FCSTD DOCUMENT  (FreeCAD 0.19R)
Label: SpokePattern32
License: All rights reserved
LicenseURL: http://en.wikipedia.org/wiki/All_rights_reserved
objects: Sketcher::SketchObject×1
note: 1 computed .brp shape members not serialized (recipe doc carries the construction recipe); baked Part::Feature solids carry a one-line shape summary decoded from their .brp

FEATURE [Sketcher::SketchObject] Sketch
  FullyConstrained = false
  sketch-geometry (69):
    g0: Circle CenterX=30 CenterY=0 CenterZ=0 NormalX=0 NormalY=0 NormalZ=1 AngleXU=0 Radius=1.25
    g1: Circle CenterX=21.2132 CenterY=21.2132 CenterZ=0 NormalX=0 NormalY=0 NormalZ=1 AngleXU=0 Radius=1.25
    g2: Circle CenterX=11.4805 CenterY=27.7164 CenterZ=0 NormalX=0 NormalY=0 NormalZ=1 AngleXU=0 Radius=1.25
    g3: Circle CenterX=0 CenterY=30 CenterZ=0 NormalX=0 NormalY=0 NormalZ=1 AngleXU=0 Radius=1.25
    g4: Circle CenterX=1.54e-14 CenterY=-30 CenterZ=0 NormalX=0 NormalY=0 NormalZ=1 AngleXU=0 Radius=1.25
    g5: Circle CenterX=-27.7164 CenterY=11.4805 CenterZ=0 NormalX=0 NormalY=0 NormalZ=1 AngleXU=0 Radius=1.25
    g6: Circle CenterX=-27.7164 CenterY=-11.4805 CenterZ=0 NormalX=0 NormalY=0 NormalZ=1 AngleXU=0 Radius=1.25
    g7: Circle CenterX=-11.4805 CenterY=27.7164 CenterZ=0 NormalX=0 NormalY=0 NormalZ=1 AngleXU=0 Radius=1.25
    g8: Circle CenterX=-30 CenterY=-3.2e-15 CenterZ=0 NormalX=0 NormalY=0 NormalZ=1 AngleXU=0 Radius=1.25
    g9: Circle CenterX=-21.2132 CenterY=-21.2132 CenterZ=0 NormalX=0 NormalY=0 NormalZ=1 AngleXU=0 Radius=1.25
    g10: Circle CenterX=-11.4805 CenterY=-27.7164 CenterZ=0 NormalX=0 NormalY=0 NormalZ=1 AngleXU=0 Radius=1.25
    g11: Circle CenterX=11.4805 CenterY=-27.7164 CenterZ=0 NormalX=0 NormalY=0 NormalZ=1 AngleXU=0 Radius=1.25
    g12: Circle CenterX=21.2132 CenterY=-21.2132 CenterZ=0 NormalX=0 NormalY=0 NormalZ=1 AngleXU=0 Radius=1.25
    g13: Circle CenterX=27.7164 CenterY=-11.4805 CenterZ=0 NormalX=0 NormalY=0 NormalZ=1 AngleXU=0 Radius=1.25
    g14: Circle CenterX=30 CenterY=1.24e-14 CenterZ=0 NormalX=0 NormalY=0 NormalZ=1 AngleXU=0 Radius=1.25
    g15: Circle CenterX=27.7164 CenterY=11.4805 CenterZ=0 NormalX=0 NormalY=0 NormalZ=1 AngleXU=0 Radius=1.25
    g16: Circle CenterX=0 CenterY=0 CenterZ=0 NormalX=0 NormalY=0 NormalZ=1 AngleXU=0 Radius=30
    g17: LineSegment StartX=-11.4805 StartY=27.7164 StartZ=0 EndX=0 EndY=0 EndZ=0
    g18: LineSegment StartX=-27.7164 StartY=11.4805 StartZ=0 EndX=0 EndY=0 EndZ=0
    g19: LineSegment StartX=21.2132 StartY=-21.2132 StartZ=0 EndX=0 EndY=0 EndZ=0
    g20: LineSegment StartX=27.7164 StartY=-11.4805 StartZ=0 EndX=0 EndY=0 EndZ=0
    g21: LineSegment StartX=30 StartY=1.24e-14 StartZ=0 EndX=0 EndY=0 EndZ=0
    g22: LineSegment StartX=27.7164 StartY=11.4805 StartZ=0 EndX=0 EndY=0 EndZ=0
    g23: LineSegment StartX=30 StartY=0 StartZ=0 EndX=0 EndY=0 EndZ=0
    g24: LineSegment StartX=11.4805 StartY=27.7164 StartZ=0 EndX=0 EndY=0 EndZ=0
    g25: LineSegment StartX=0 StartY=30 StartZ=0 EndX=0 EndY=0 EndZ=0
    g26: LineSegment StartX=21.2132 StartY=21.2132 StartZ=0 EndX=0 EndY=0 EndZ=0
    g27: LineSegment StartX=30 StartY=0 StartZ=0 EndX=0 EndY=0 EndZ=0
    g28: LineSegment StartX=11.4805 StartY=-27.7164 StartZ=0 EndX=0 EndY=0 EndZ=0
    g29: LineSegment StartX=1.54e-14 StartY=-30 StartZ=0 EndX=0 EndY=0 EndZ=0
    g30: LineSegment StartX=-21.2132 StartY=-21.2132 StartZ=0 EndX=0 EndY=0 EndZ=0
    g31: LineSegment StartX=-11.4805 StartY=-27.7164 StartZ=0 EndX=0 EndY=0 EndZ=0
    g32: LineSegment StartX=-27.7164 StartY=-11.4805 StartZ=0 EndX=0 EndY=0 EndZ=0
    g33: LineSegment StartX=-30 StartY=-3.2e-15 StartZ=0 EndX=0 EndY=0 EndZ=0
    g34: Circle CenterX=-21.2132 CenterY=21.2132 CenterZ=0 NormalX=0 NormalY=0 NormalZ=1 AngleXU=0 Radius=1.25
    g35: LineSegment StartX=-21.2132 StartY=21.2132 StartZ=0 EndX=0 EndY=0 EndZ=0
    g36: Circle CenterX=0 CenterY=0 CenterZ=0 NormalX=0 NormalY=0 NormalZ=1 AngleXU=0 Radius=137.253
    g37: Circle CenterX=-59.5517 CenterY=123.66 CenterZ=0 NormalX=0 NormalY=0 NormalZ=1 AngleXU=0 Radius=2
    g38: Circle CenterX=-2.13e-14 CenterY=137.253 CenterZ=0 NormalX=0 NormalY=0 NormalZ=1 AngleXU=0 Radius=2
    g39: Circle CenterX=59.5517 CenterY=123.66 CenterZ=0 NormalX=0 NormalY=0 NormalZ=1 AngleXU=0 Radius=2
    g40: Circle CenterX=107.309 CenterY=85.5757 CenterZ=0 NormalX=0 NormalY=0 NormalZ=1 AngleXU=0 Radius=2
    g41: Circle CenterX=133.812 CenterY=30.5416 CenterZ=0 NormalX=0 NormalY=0 NormalZ=1 AngleXU=0 Radius=2
    g42: Circle CenterX=133.812 CenterY=-30.5416 CenterZ=0 NormalX=0 NormalY=0 NormalZ=1 AngleXU=0 Radius=2
    g43: Circle CenterX=107.309 CenterY=-85.5757 CenterZ=0 NormalX=0 NormalY=0 NormalZ=1 AngleXU=0 Radius=2
    g44: Circle CenterX=59.5517 CenterY=-123.66 CenterZ=0 NormalX=0 NormalY=0 NormalZ=1 AngleXU=0 Radius=2
    g45: Circle CenterX=3.5e-14 CenterY=-137.253 CenterZ=0 NormalX=0 NormalY=0 NormalZ=1 AngleXU=0 Radius=2
    g46: Circle CenterX=-59.5517 CenterY=-123.66 CenterZ=0 NormalX=0 NormalY=0 NormalZ=1 AngleXU=0 Radius=2
    g47: Circle CenterX=-107.309 CenterY=-85.5757 CenterZ=0 NormalX=0 NormalY=0 NormalZ=1 AngleXU=0 Radius=2
    g48: Circle CenterX=-59.5517 CenterY=-123.66 CenterZ=0 NormalX=0 NormalY=0 NormalZ=1 AngleXU=0 Radius=2
    g49: Circle CenterX=-107.309 CenterY=-85.5757 CenterZ=0 NormalX=0 NormalY=0 NormalZ=1 AngleXU=0 Radius=2
    g50: Circle CenterX=-133.812 CenterY=-30.5416 CenterZ=0 NormalX=0 NormalY=0 NormalZ=1 AngleXU=0 Radius=2
    g51: Circle CenterX=-133.812 CenterY=30.5416 CenterZ=0 NormalX=0 NormalY=0 NormalZ=1 AngleXU=0 Radius=2
    g52: Circle CenterX=-107.309 CenterY=85.5757 CenterZ=0 NormalX=0 NormalY=0 NormalZ=1 AngleXU=0 Radius=2
    g53: LineSegment StartX=-107.309 StartY=85.5757 StartZ=0 EndX=-59.5517 EndY=123.66 EndZ=0
    g54: LineSegment StartX=-59.5517 StartY=123.66 StartZ=0 EndX=-2.13e-14 EndY=137.253 EndZ=0
    g55: LineSegment StartX=-2.13e-14 StartY=137.253 StartZ=0 EndX=59.5517 EndY=123.66 EndZ=0
    g56: LineSegment StartX=59.5517 StartY=123.66 StartZ=0 EndX=107.309 EndY=85.5757 EndZ=0
    g57: LineSegment StartX=107.309 StartY=85.5757 StartZ=0 EndX=133.812 EndY=30.5416 EndZ=0
    g58: LineSegment StartX=133.812 StartY=30.5416 StartZ=0 EndX=133.812 EndY=-30.5416 EndZ=0
    g59: LineSegment StartX=133.812 StartY=-30.5416 StartZ=0 EndX=107.309 EndY=-85.5757 EndZ=0
    g60: LineSegment StartX=107.309 StartY=-85.5757 StartZ=0 EndX=59.5517 EndY=-123.66 EndZ=0
    g61: LineSegment StartX=59.5517 StartY=-123.66 StartZ=0 EndX=3.55e-14 EndY=-137.253 EndZ=0
    g62: LineSegment StartX=3.5e-14 StartY=-137.253 StartZ=0 EndX=-59.5517 EndY=-123.66 EndZ=0
    g63: LineSegment StartX=-59.5517 StartY=-123.66 StartZ=0 EndX=-107.309 EndY=-85.5757 EndZ=0
    g64: LineSegment StartX=-107.309 StartY=-85.5757 StartZ=0 EndX=-59.5517 EndY=-123.66 EndZ=0
    g65: LineSegment StartX=-59.5517 StartY=-123.66 StartZ=0 EndX=-107.309 EndY=-85.5757 EndZ=0
    g66: LineSegment StartX=-107.309 StartY=-85.5757 StartZ=0 EndX=-133.812 EndY=-30.5416 EndZ=0
    g67: LineSegment StartX=-133.812 StartY=-30.5416 StartZ=0 EndX=-133.812 EndY=30.5416 EndZ=0
    g68: LineSegment StartX=-133.812 StartY=30.5416 StartZ=0 EndX=-107.309 EndY=85.5757 EndZ=0
  constraints (143):
    c: PointOnObject(g0,g-1)
    c: DistanceX(g0) = 30
    c: Diameter(g0) = 2.5
    c: Diameter(g1) = 2.5
    c: Equal(g1, g2-g15) x14
    c: Coincident(g16,g-1)
    c: PointOnObject(g9,g16)
    c: PointOnObject(g12,g16)
    c: PointOnObject(g13,g16)
    c: PointOnObject(g11,g16)
    c: PointOnObject(g7,g16)
    c: PointOnObject(g6,g16)
    c: PointOnObject(g5,g16)
    c: PointOnObject(g10,g16)
    c: PointOnObject(g8,g16)
    c: PointOnObject(g4,g16)
    c: PointOnObject(g3,g16)
    c: PointOnObject(g2,g16)
    c: PointOnObject(g15,g16)
    c: PointOnObject(g14,g16)
    c: PointOnObject(g0,g16)
    c: Coincident(g17,g7)
    c: Coincident(g17,g16)
    c: Coincident(g18,g5)
    c: Coincident(g18,g16)
    c: Coincident(g19,g12)
    c: Coincident(g19,g16)
    c: Coincident(g20,g13)
    c: Coincident(g20,g16)
    c: Coincident(g21,g14)
    c: Coincident(g21,g16)
    c: Coincident(g22,g15)
    c: Coincident(g22,g16)
    c: Coincident(g23,g0)
    c: Coincident(g23,g16)
    c: Coincident(g24,g2)
    c: Coincident(g24,g16)
    c: Coincident(g25,g3)
    c: Coincident(g25,g16)
    c: Vertical(g25)
    c: Coincident(g26,g1)
    c: Coincident(g26,g16)
    c: Coincident(g27,g0)
    c: Coincident(g27,g16)
    c: Coincident(g28,g11)
    c: Coincident(g28,g16)
    c: Coincident(g29,g4)
    c: Coincident(g29,g16)
    c: Coincident(g30,g9)
    c: Coincident(g30,g16)
    c: Coincident(g31,g16)
    c: Angle(g26,g24) = 0.392699
    c: Angle(g22,g26) = 0.392699
    c: Angle(g21,g22) = 0.392699
    c: Angle(g20,g21) = 0.392699
    c: Angle(g19,g20) = 0.392699
    c: Angle(g28,g19) = 0.392699
    c: Angle(g29,g28) = 0.392699
    c: Coincident(g10,g31)
    c: Angle(g31,g29) = 0.392699
    c: Angle(g30,g31) = 0.392699
    c: Coincident(g32,g6)
    c: Coincident(g32,g16)
    c: Coincident(g33,g8)
    c: Coincident(g33,g16)
    c: Angle(g32,g30) = 0.392699
    c: Angle(g33,g32) = 0.392699
    c: Angle(g18,g33) = 0.392699
    c: Angle(g24,g25) = 0.392699
    c: Angle(g25,g17) = 0.392699
    c: PointOnObject(g34,g16)
    c: Coincident(g35,g34)
    c: Coincident(g35,g16)
    c: Angle(g35,g18) = 0.392699
    c: PointOnObject(g1,g16)
    c: Diameter(g34) = 2.5
    c: Coincident(g36,g16)
    c: Diameter(g37) = 4
    c: Equal(g37, g38-g52) x15
    c: PointOnObject(g37,g36)
    c: PointOnObject(g38,g36)
    c: PointOnObject(g39,g36)
    c: PointOnObject(g40,g36)
    c: PointOnObject(g41,g36)
    c: PointOnObject(g42,g36)
    c: PointOnObject(g43,g36)
    c: PointOnObject(g44,g36)
    c: PointOnObject(g45,g36)
    c: PointOnObject(g46,g36)
    c: PointOnObject(g47,g36)
    c: PointOnObject(g48,g36)
    c: PointOnObject(g49,g36)
    c: PointOnObject(g50,g36)
    c: PointOnObject(g51,g36)
    c: PointOnObject(g52,g36)
    c: Coincident(g53,g52)
    c: Coincident(g53,g37)
    c: Coincident(g54,g37)
    c: Coincident(g54,g38)
    c: Coincident(g55,g38)
    c: Coincident(g55,g39)
    c: Coincident(g56,g39)
    c: Coincident(g56,g40)
    c: Coincident(g57,g40)
    c: Coincident(g57,g41)
    c: Coincident(g58,g41)
    c: Coincident(g58,g42)
    c: Vertical(g58)
    c: Coincident(g59,g42)
    c: Coincident(g59,g43)
    c: Coincident(g60,g43)
    c: Coincident(g60,g44)
    c: Coincident(g61,g44)
    c: Coincident(g61,g45)
    c: Coincident(g62,g45)
    c: Coincident(g62,g46)
    c: Coincident(g63,g46)
    c: Coincident(g63,g47)
    c: Coincident(g64,g47)
    c: Coincident(g64,g48)
    c: Coincident(g65,g48)
    c: Coincident(g65,g49)
    c: Coincident(g66,g49)
    c: Coincident(g66,g50)
    c: Coincident(g67,g50)
    c: Coincident(g67,g51)
    c: Vertical(g67)
    c: Coincident(g68,g51)
    c: Coincident(g68,g52)
    c: Equal(g53,g54)
    c: Equal(g54,g55)
    c: Equal(g55,g56)
    c: Equal(g56,g57)
    c: Equal(g57,g58)
    c: Equal(g58,g59)
    c: Equal(g59,g60)
    c: Equal(g60,g61)
    c: Equal(g61,g62)
    c: Equal(g62,g63)
    c: Equal(g63,g64)
    c: Equal(g64,g65)
    c: Equal(g65,g66)
    c: Equal(g66,g67)
